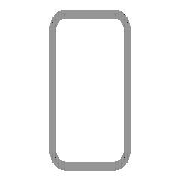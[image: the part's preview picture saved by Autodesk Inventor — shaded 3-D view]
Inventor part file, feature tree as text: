
AUTODESK INVENTOR PART (.ipt)
format: ipt  version: 2025 (Build 290162010, 162A)  size: 142,336 bytes
history: native  units: mm (DEFAULTED — no unit token found)
features: other x4, plane x2, split x1, sketch x1
ambient origin geometry x8: Origin, YZ Plane, XZ Plane, XY Plane, X Axis, Y Axis, Z Axis, Center Point
bodies: Solid1 (feature_tree), Body (feature_tree)
feature tree (8):
  parser-record x1  (decoder bookkeeping rows leaked as tree rows — omitted from the tree; the rows remain in map.json)
  other  "Driven Length"
  other  "Start Plane"
  other  "End Plane"
  plane  "Work Plane4"
  split  "Split1"
  sketch  "Sketch3"  dims[d3=608.634757mm d4=0.0mm d7=4.0mm d9=20.0mm d11=40.0mm d12=2.0mm d13=-0.0mm d14=608.634757mm d15=10.0mm d16=20.0mm d17=90.0deg d18=608.634757mm]
  plane  "Work Plane3"
